# Revit family: RHK2_63_UN_Inlay LED_ETK
name_source: partatom
category: Lighting Fixtures
units: mm (PartAtom-declared; Revit-internal decimal feet)

## family parameters
Always vertical = Yes
Cut with Voids When Loaded = No
Light Source = No
OmniClass Number = 23.80.70.11.14.11
OmniClass Title = Downlights
Part Type = Normal
Room Calculation Point = Yes
Round Connector Dimension = Use Diameter
Shared = No
Work Plane-Based = No

## types (8) — shared parameters
Assembly Code = 63.0
Description = Recessed/inlay LED
IfcExportAs = IfcLightFixtureType
IfcExportType = USERDEFINED
Lamp = LED
Luminaire_Body_Material = Plastic, Opaque White
Manufacturer = ETK licht B.V.
Model = RHK.2
URL = https://www.etk.nl
Voltage = 230 V
Width = 148 mm

## per-type parameters (varying)
| type | Apparent Load | Length | Light Source | Reflectors | Wattage Comments |
| RHK.2000.15 - 16W / 2200lm / 3000K | 16 VA | 1197 mm | RHK.2 - Lightsource : RHK.2000.15 - 16W / 2200lm / 3000K | 27 | 16W |
| RHK.2100.15 - 16W / 2300lm / 4000K | 16 VA | 1197 mm | RHK.2 - Lightsource : RHK.2100.15 - 16W / 2300lm / 4000K | 27 | 16W |
| RHK.2200.15 - 31W / 4000lm / 3000K | 31 VA | 1197 mm | RHK.2 - Lightsource : RHK.2200.15 - 31W / 4000lm / 3000K | 27 | 31W |
| RHK.2300.15 - 31W / 4200lm / 4000K | 31 VA | 1197 mm | RHK.2 - Lightsource : RHK.2300.15 - 31W / 4200lm / 4000K | 27 | 31W |
| RHK.2400.15 - 37W / 4850lm / 3000K | 37 VA | 1470 mm | RHK.2 - Lightsource : RHK.2400.15 - 37W / 4850lm / 3000K | 33 | 37W |
| RHK.2500.15 - 37W / 5100lm / 4000K | 37 VA | 1470 mm | RHK.2 - Lightsource : RHK.2500.15 - 37W / 5100lm / 4000K | 33 | 37W |
| RHK.2600.15 - 48W / 6250lm / 3000K | 37 VA | 1470 mm | RHK.2 - Lightsource : RHK.2600.15 - 48W / 6250lm / 3000K | 33 | 37W |
| RHK.2700.15 - 48W / 6550lm / 4000K | 37 VA | 1470 mm | RHK.2 - Lightsource : RHK.2700.15 - 48W / 6550lm / 4000K | 33 | 37W |

## geometry (parser evidence)
native form markers: Sweep x7
no freeform markers — native parametric forms only
